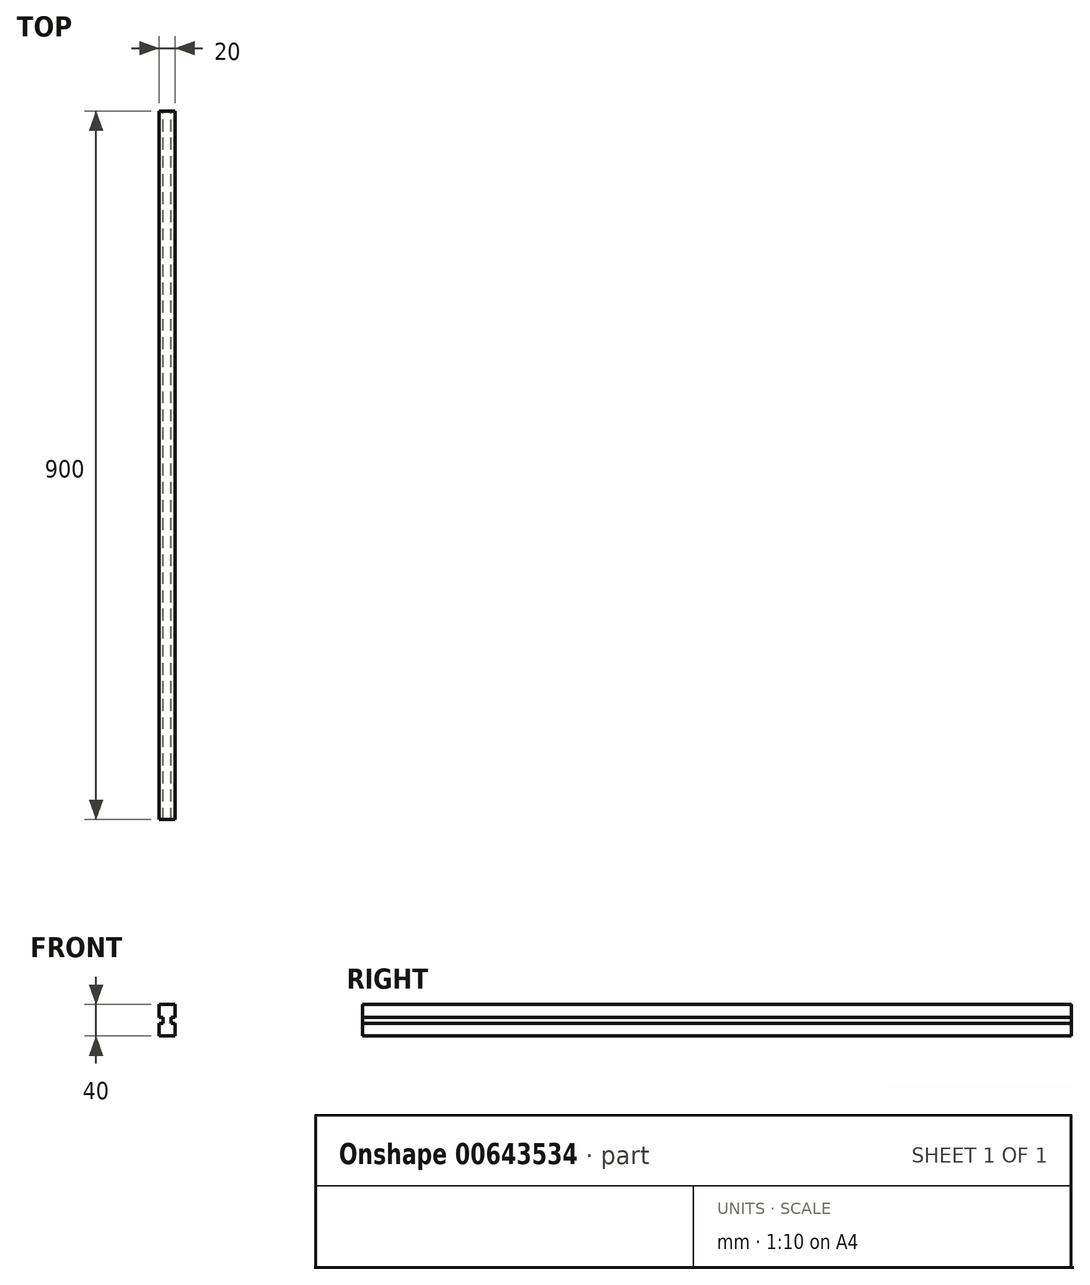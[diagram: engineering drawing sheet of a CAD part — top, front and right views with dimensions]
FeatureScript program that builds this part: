
annotation { "Feature Type Name" : "Feature", "Feature Type Description" : "" }
export const myFeature = defineFeature(function(context is Context, id is Id, definition is map)
    precondition{}
    {
        {
            var Q0;
            Q0=qCreatedBy(makeId("Front.planeOp"),FACE);
            var sketch = newSketch(context, id + "F0", { "sketchPlane" : qUnion([Q0])});
            skLineSegment(sketch, "E0.bottom", {"start": v(10, -20) * mm, "end": v(-10, -20) * mm});
            skLineSegment(sketch, "E0.top", {"start": v(10, 20) * mm, "end": v(-10, 20) * mm});
            skLineSegment(sketch, "E0.left", {"start": v(10, -20) * mm, "end": v(10, -4) * mm});
            skLineSegment(sketch, "E0.right", {"start": v(-10, -20) * mm, "end": v(-10, -4) * mm});
            skPoint(sketch, "E0.middle", {"position": v(0, 0) * mm});
            skLineSegment(sketch, "E1.bottom", {"start": v(10, 4) * mm, "end": v(5, 4) * mm});
            skLineSegment(sketch, "E1.top", {"start": v(10, -4) * mm, "end": v(5, -4) * mm});
            skLineSegment(sketch, "E1.right", {"start": v(5, 4) * mm, "end": v(5, -4) * mm});
            skLineSegment(sketch, "E2.bottom", {"start": v(-10, 4) * mm, "end": v(-5, 4) * mm});
            skLineSegment(sketch, "E2.top", {"start": v(-10, -4) * mm, "end": v(-5, -4) * mm});
            skLineSegment(sketch, "E2.right", {"start": v(-5, 4) * mm, "end": v(-5, -4) * mm});
            skLineSegment(sketch, "E3.trimOffspring", {"start": v(-10, 4) * mm, "end": v(-10, 20) * mm});
            skLineSegment(sketch, "E4.trimOffspring", {"start": v(10, 4) * mm, "end": v(10, 20) * mm});
            skSolve(sketch);
        }
        {
            var Q0;
            Q0 = qSketchRegion(id + "F0", true);
            extrude(context, id + "F1", {"entities" : qUnion([Q0]), "depth" : 400 * mm, "offsetDistance" : 25 * mm, "hasSecondDirection" : true, "secondDirectionOppositeDirection" : true, "secondDirectionDepth" : 500 * mm});
        }
    });
